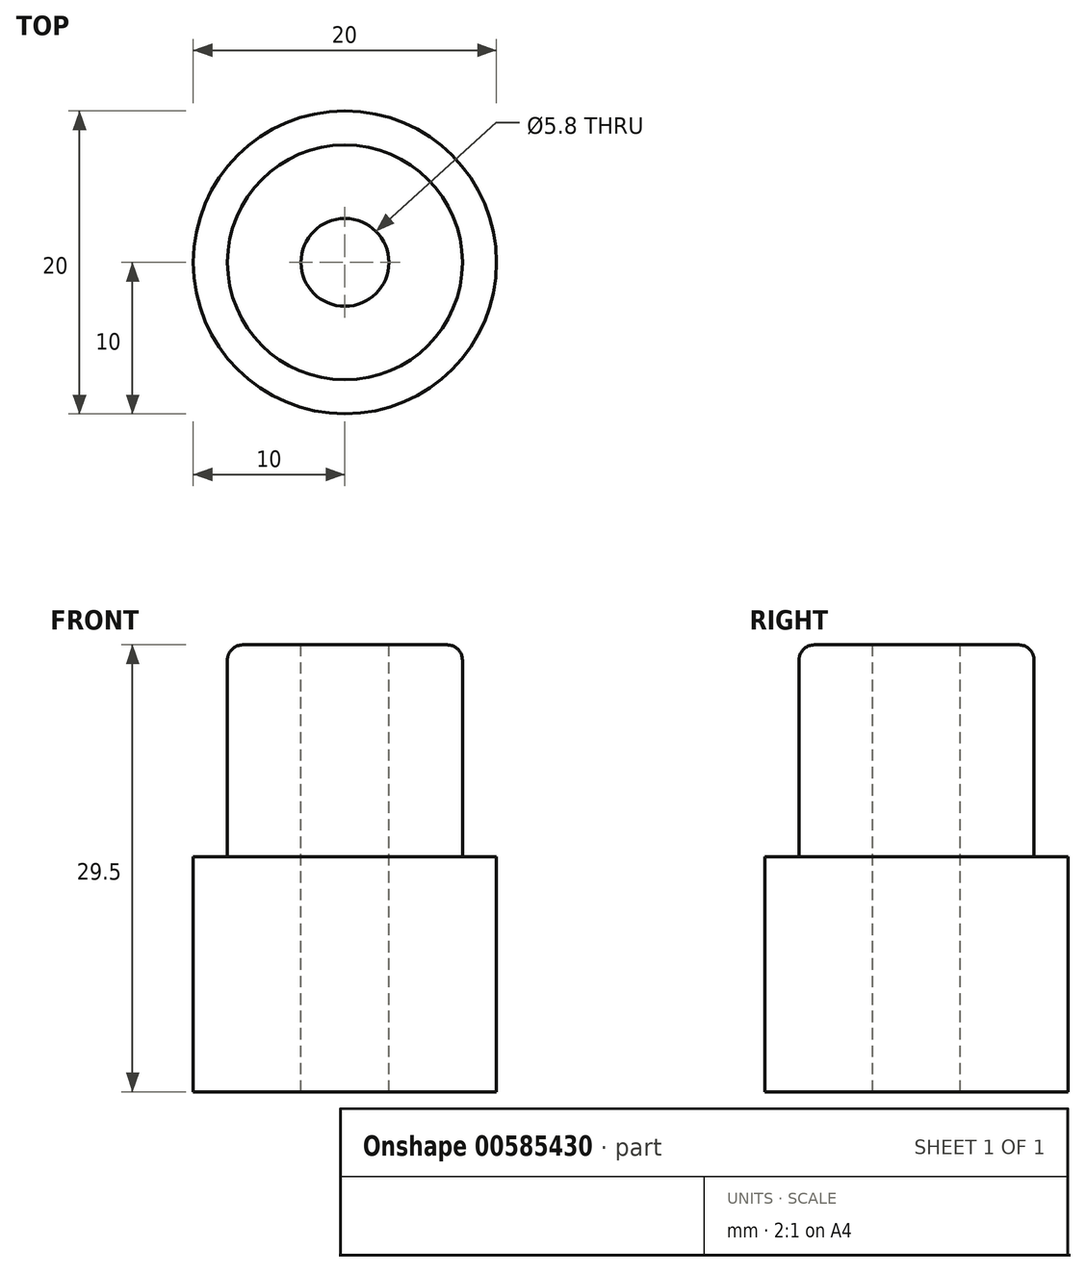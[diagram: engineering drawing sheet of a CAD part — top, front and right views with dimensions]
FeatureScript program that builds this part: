
annotation { "Feature Type Name" : "Feature", "Feature Type Description" : "" }
export const myFeature = defineFeature(function(context is Context, id is Id, definition is map)
    precondition{}
    {
        {
            var Q0;
            Q0=qCreatedBy(makeId("Top.planeOp"),FACE);
            var sketch = newSketch(context, id + "F0", { "sketchPlane" : qUnion([Q0])});
            skCircle(sketch, "E0", {"center": v(0, 0) * mm, "radius": 10 * mm});
            skSolve(sketch);
        }
        {
            var Q0;
            Q0 = qSketchRegion(id + "F0", true);
            extrude(context, id + "F1", {"entities" : qUnion([Q0]), "depth" : 15.5 * mm, "offsetDistance" : 25 * mm});
        }
        {
            var Q0;
            Q0=makeQuery(id+"F1.opExtrude","CAP_FACE",FACE,{"disambiguationData":[OSD([sQuery(id+"F0.wireOp",EDGE,"E0")])],"isStart":false});
            var sketch = newSketch(context, id + "F2", { "sketchPlane" : qUnion([Q0])});
            skCircle(sketch, "E1", {"center": v(0, 0) * mm, "radius": 7.75 * mm});
            skSolve(sketch);
        }
        {
            var Q0;
            Q0 = qSketchRegion(id + "F2", true);
            extrude(context, id + "F3", {"entities" : qUnion([Q0]), "operationType" : NewBodyOperationType.ADD, "depth" : 14 * mm, "offsetDistance" : 25 * mm});
        }
        {
            var Q0;
            Q0=makeQuery(id+"F3.opExtrude","CAP_FACE",FACE,{"disambiguationData":[OSD([sQuery(id+"F2.wireOp",EDGE,"E1")])],"isStart":false});
            var sketch = newSketch(context, id + "F4", { "sketchPlane" : qUnion([Q0])});
            skCircle(sketch, "E2", {"center": v(0, 0) * mm, "radius": 2.9 * mm});
            skSolve(sketch);
        }
        {
            var Q0;
            Q0 = qSketchRegion(id + "F4", true);
            extrude(context, id + "F5", {"entities" : qUnion([Q0]), "operationType" : NewBodyOperationType.REMOVE, "oppositeDirection" : true, "depth" : 31 * mm, "offsetDistance" : 25 * mm});
        }
        {
            var Q0;
            Q0=makeQuery(id+"F3.opExtrude","CAP_EDGE",EDGE,{"disambiguationData":[OSD([sQuery(id+"F2.wireOp",EDGE,"E1")])],"isStart":false});
            fillet(context, id + "F6", {"entities" : qUnion([Q0]), "radius" : 1 * mm, "tangentPropagation" : true, "allowEdgeOverflow" : false});
        }
    });
